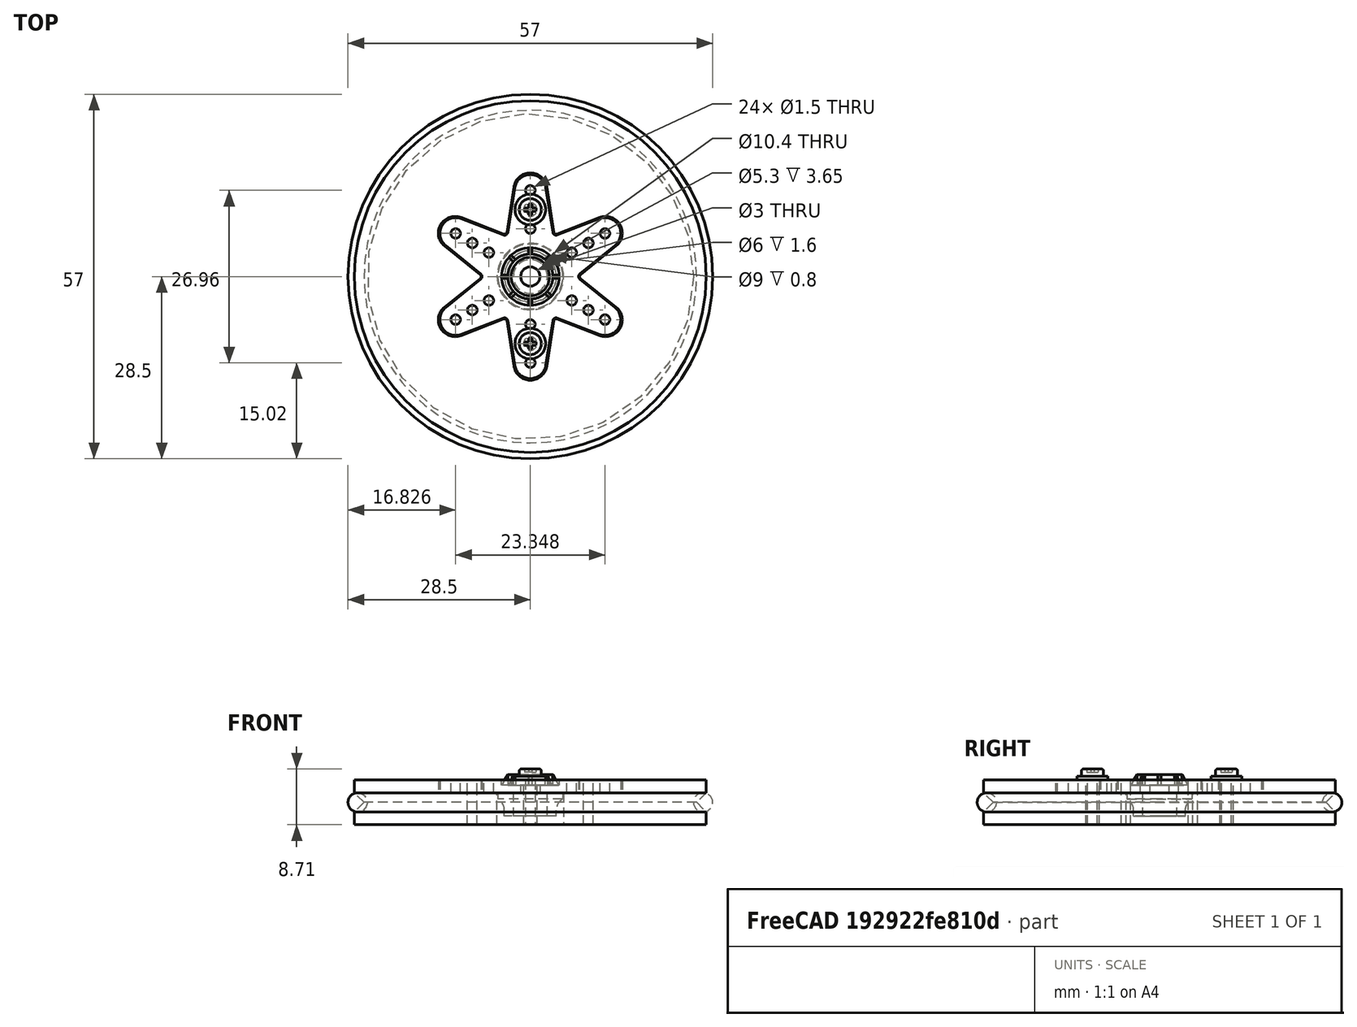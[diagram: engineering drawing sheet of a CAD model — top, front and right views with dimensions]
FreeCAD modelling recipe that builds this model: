
FCSTD DOCUMENT  (FreeCAD 0.14R3702 (Git))
Label: Miniskybot-wheel-futaba3003-6-arms-horn-assembly
License: CC-BY 3.0
LicenseURL: http://creativecommons.org/licenses/by/3.0/
objects: Part::Feature×4, Part::Torus×1, Part::Compound×1
note: 6 computed .brp shape members not serialized (recipe doc carries the construction recipe); baked Part::Feature solids carry a one-line shape summary decoded from their .brp

FEATURE [Part::Feature] PolarPattern001  label="Wheel-futaba-30036-6-arms-horn-final"
  shape: bbox 55 x 55 x 7 mm, 40 faces (baked)
FEATURE [Part::Feature] PolarPattern002  label="6-arms-horn-final001"
  Placement = pos=(0,0,1.51) rot=(0,0,1;0rad)
  shape: bbox 28.28 x 31.9 x 6.973 mm, 93 faces (baked)
FEATURE [Part::Torus] Torus  label="o-ring"
  Angle1 = -180
  Angle2 = 180
  Angle3 = 360
  Radius1 = 27
  Radius2 = 1.5
FEATURE [Part::Feature] Fillet  label="bolt-1"
  Placement = pos=(0,10.48,3.51) rot=(0,0,1;0rad)
  shape: bbox 4.8 x 4.8 x 8.7 mm, 21 faces (baked)
FEATURE [Part::Feature] Fillet001  label="bolt-002"
  Placement = pos=(0,-10.48,3.51) rot=(0,0,1;0rad)
  shape: bbox 4.8 x 4.8 x 8.7 mm, 21 faces (baked)
FEATURE [Part::Compound] Compound  label="Miniskybot-wheel-futaba3003-6-arms-horn-assembly"
  Links = -> [Fillet001,PolarPattern001,PolarPattern002,Torus,Fillet]
